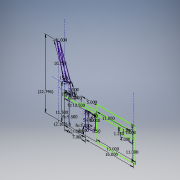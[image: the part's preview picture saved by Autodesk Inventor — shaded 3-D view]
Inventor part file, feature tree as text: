
AUTODESK INVENTOR PART (.ipt)
format: ipt  version: 2017 SP1 (Build 210196100, 196)  size: 140,800 bytes
history: native  units: in
note: dims shown in document units (in); Inventor stores cm internally (conversion verified against a paired STEP export)
features: sketch x1
ambient origin geometry x8: Origin, YZ Plane, XZ Plane, XY Plane, X Axis, Y Axis, Z Axis, Center Point
feature tree (1):
  sketch  "Sketch1"  dims[d0=2.5in d1=5.0in d2=1.25in d3=0.75in d4=16.0in d7=5.0in d8=8.0in d9=5.0in d10=10.5in d11=0.25in d12=13.0in d13=11.0in d14=3.0in d17=3.5in d19=2.0in d20=11.0in d22=1.25in d23=4.0in d24=1.0in d25=7.0in d30=1.0in d31=4.5in d34=11.5in d36=1.0in d38=1.2in d39=1.5in d40=9.5in d41=7.0in d42=5.0in d44=1.0in d45=10.75in d46=3.5in d51=15.0deg d52=2.749in d53=2.7461in d57=2.1823in d58=22.7456in d59=0.125in]
